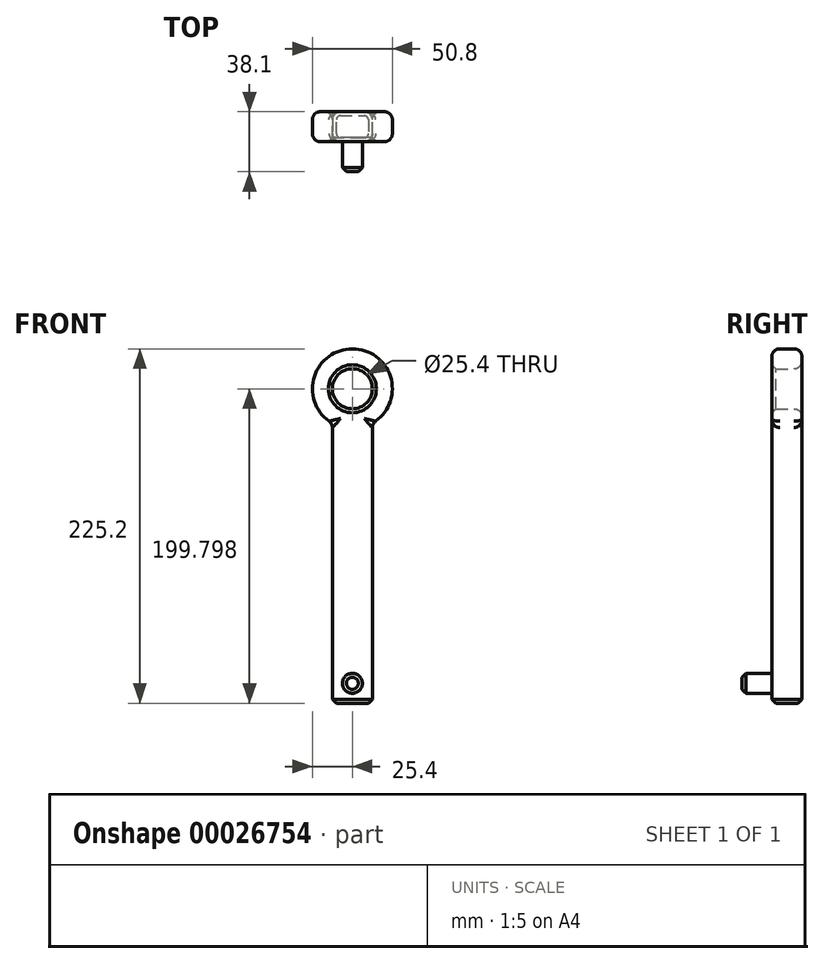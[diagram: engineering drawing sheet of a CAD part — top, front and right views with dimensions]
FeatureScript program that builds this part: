
annotation { "Feature Type Name" : "Feature", "Feature Type Description" : "" }
export const myFeature = defineFeature(function(context is Context, id is Id, definition is map)
    precondition{}
    {
        {
            var Q0;
            Q0=qCreatedBy(makeId("Front.planeOp"),FACE);
            var sketch = newSketch(context, id + "F0", { "sketchPlane" : qUnion([Q0])});
            skLineSegment(sketch, "E0.rect.bottom", {"start": v(12.7, -99.9) * mm, "end": v(-12.7, -99.9) * mm});
            skLineSegment(sketch, "E0.rect.left", {"start": v(12.7, -99.9) * mm, "end": v(12.7, 77.9) * mm});
            skLineSegment(sketch, "E0.rect.right", {"start": v(-12.7, -99.9) * mm, "end": v(-12.7, 77.9) * mm});
            skPoint(sketch, "E0.rect.middle", {"position": v(0, 0) * mm});
            skArc(sketch, "E1", {"start": v(12.7, 77.9) * mm, "mid": v(0, 125.3) * mm, "end": v(-12.7, 77.9) * mm});
            skPoint(sketch, "E2.orphan", {"position": v(-12.7, 99.9) * mm});
            skPoint(sketch, "E3.orphan", {"position": v(12.7, 99.9) * mm});
            skCircle(sketch, "E4", {"center": v(0, 99.9) * mm, "radius": 12.7 * mm});
            skSolve(sketch);
        }
        {
            var Q0;
            Q0=makeQuery(id+"F0.imprint","IMPRINT",FACE,{"disambiguationData":[TD([[makeQuery(id+"F0.imprint","IMPRINT",EDGE,{"derivedFrom":sQuery(id+"F0.wireOp",EDGE,"E0.rect.bottom")}),-1.0]])]});
            extrude(context, id + "F1", {"entities" : qUnion([Q0]), "depth" : 19.05 * mm});
        }
        {
            var Q0;
            Q0=makeQuery(id+"F1.opExtrude","CAP_EDGE",EDGE,{"disambiguationData":[OSD([sQuery(id+"F0.wireOp",EDGE,"E1")])],"isStart":false});
            var Q1;
            Q1=makeQuery(id+"F1.opExtrude","CAP_EDGE",EDGE,{"disambiguationData":[OSD([sQuery(id+"F0.wireOp",EDGE,"E1")])],"isStart":true});
            var Q2;
            Q2=makeQuery(id+"F1.opExtrude","CAP_EDGE",EDGE,{"disambiguationData":[OSD([sQuery(id+"F0.wireOp",EDGE,"E0.rect.left")])],"isStart":false});
            var Q3;
            Q3=makeQuery(id+"F1.opExtrude","CAP_EDGE",EDGE,{"disambiguationData":[OSD([sQuery(id+"F0.wireOp",EDGE,"E0.rect.left")])],"isStart":true});
            var Q4;
            Q4=makeQuery(id+"F1.opExtrude","CAP_EDGE",EDGE,{"disambiguationData":[OSD([sQuery(id+"F0.wireOp",EDGE,"E0.rect.right")])],"isStart":true});
            var Q5;
            Q5=makeQuery(id+"F1.opExtrude","CAP_EDGE",EDGE,{"disambiguationData":[OSD([sQuery(id+"F0.wireOp",EDGE,"E0.rect.right")])],"isStart":false});
            fillet(context, id + "F2", {"entities" : qUnion([Q0, Q1, Q2, Q3, Q4, Q5]), "radius" : 5.08 * mm, "tangentPropagation" : true, "allowEdgeOverflow" : false});
        }
        {
            var Q0;
            Q0=makeQuery(id+"F1.opExtrude","CAP_EDGE",EDGE,{"disambiguationData":[OSD([sQuery(id+"F0.wireOp",EDGE,"E4")])],"isStart":false});
            chamfer(context, id + "F3", {"entities" : qUnion([Q0]), "width" : 2.54 * mm, "tangentPropagation" : true});
        }
        {
            var Q0;
            Q0=makeQuery(id+"F1.opExtrude","CAP_FACE",FACE,{"disambiguationData":[OSD([sQuery(id+"F0.wireOp",EDGE,"E0.rect.bottom"),sQuery(id+"F0.wireOp",EDGE,"E0.rect.left"),sQuery(id+"F0.wireOp",EDGE,"E0.rect.right"),sQuery(id+"F0.wireOp",EDGE,"E1"),sQuery(id+"F0.wireOp",EDGE,"E4")])],"isStart":false});
            var sketch = newSketch(context, id + "F4", { "sketchPlane" : qUnion([Q0])});
            skCircle(sketch, "E5", {"center": v(0, -87.2) * mm, "radius": 6.35 * mm});
            skLineSegment(sketch, "E6", {"start": v(0, -87.2) * mm, "end": v(0, -99.9) * mm});
            skSolve(sketch);
        }
        {
            var Q0;
            Q0=makeQuery(id+"F4.imprint","IMPRINT",FACE,{"disambiguationData":[TD([[makeQuery(id+"F4.imprint","IMPRINT",EDGE,{"derivedFrom":sQuery(id+"F4.wireOp",EDGE,"E5")}),1.0]])]});
            extrude(context, id + "F5", {"entities" : qUnion([Q0]), "operationType" : NewBodyOperationType.ADD, "depth" : 19.05 * mm});
        }
        {
            var Q0;
            Q0=makeQuery(id+"F5.opExtrude","CAP_EDGE",EDGE,{"disambiguationData":[OSD([sQuery(id+"F4.wireOp",EDGE,"E5")])],"isStart":false});
            chamfer(context, id + "F6", {"entities" : qUnion([Q0]), "width" : 2.54 * mm, "tangentPropagation" : true});
        }
        {
            var Q0;
            Q0=makeQuery(id+"F1.opExtrude","CAP_EDGE",EDGE,{"disambiguationData":[OSD([sQuery(id+"F0.wireOp",EDGE,"E4")])],"isStart":true});
            fillet(context, id + "F7", {"entities" : qUnion([Q0]), "radius" : 5.08 * mm, "tangentPropagation" : true, "allowEdgeOverflow" : false});
        }
        {
            var Q0;
            Q0=makeQuery(id+"F1.opExtrude","SWEPT_EDGE",EDGE,{"disambiguationData":[OSD([sQuery(id+"F0.wireOp",EDGE,"E0.rect.left"),sQuery(id+"F0.wireOp",EDGE,"E1")])]});
            var Q1;
            Q1=makeQuery(id+"F1.opExtrude","SWEPT_EDGE",EDGE,{"disambiguationData":[OSD([sQuery(id+"F0.wireOp",EDGE,"E0.rect.right"),sQuery(id+"F0.wireOp",EDGE,"E1")])]});
            var Q2;
            Q2=makeQuery(id+"F5.opExtrude","CAP_EDGE",EDGE,{"disambiguationData":[OSD([sQuery(id+"F4.wireOp",EDGE,"E5")])],"isStart":true});
            fillet(context, id + "F8", {"entities" : qUnion([Q0, Q1, Q2]), "radius" : 5.08 * mm, "tangentPropagation" : true, "allowEdgeOverflow" : false});
        }
        {
            var Q0;
            Q0=makeQuery(id+"F1.opExtrude","CAP_EDGE",EDGE,{"disambiguationData":[OSD([sQuery(id+"F0.wireOp",EDGE,"E0.rect.bottom")])],"isStart":false});
            chamfer(context, id + "F9", {"entities" : qUnion([Q0]), "width" : 2.54 * mm, "tangentPropagation" : true});
        }
    });
